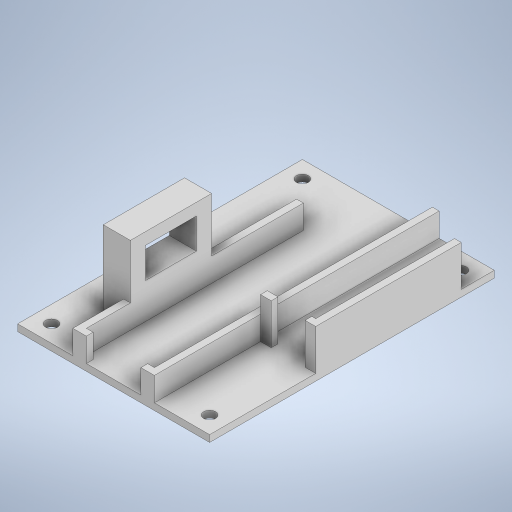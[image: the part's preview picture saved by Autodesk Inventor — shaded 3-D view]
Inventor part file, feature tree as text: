
AUTODESK INVENTOR PART (.ipt)
format: ipt  version: 2023 (Build 270158000, 158)  size: 385,024 bytes
history: native  units: mm
features: extrude x8, sketch x8, other x1
ambient origin geometry x8: Origin, YZ Plane, XZ Plane, XY Plane, X Axis, Y Axis, Z Axis, Center Point
bodies: Body1 (feature_tree)
feature tree (17):
  other  "Sólido1"
  extrude  "Extrusión1"  Depth=20.1mm
  extrude  "Extrusión2"  Depth=2.0mm TaperAngle=0.0deg
  extrude  "Extrusión5"  Depth=7.0mm TaperAngle=0.0deg
  extrude  "Extrusión6"  Depth=15.0mm
  extrude  "Extrusión8"  Depth=2.0mm
  extrude  "Extrusión10"  Depth=4.0mm
  extrude  "Extrusión11"  Depth=14.3mm
  extrude  "Extrusión12"  TaperAngle=0.0deg  [1 undecoded]
  sketch  "Boceto1"  dims[d0=20.1mm d1=80.1mm]
  sketch  "Boceto2"  dims[d2=2.0mm d3=2.0mm d4=0.0mm]
  sketch  "Boceto5"  dims[d5=2.0mm d6=7.0mm d7=0.0mm]
  sketch  "Boceto6"  dims[d8=18.0mm d9=15.0mm]
  sketch  "Boceto8"  dims[d10=12.362696mm d11=2.0mm]
  sketch  "Boceto10"  dims[d12=2.0mm d13=4.0mm]
  sketch  "Boceto11"  dims[d14=4.0mm d25=14.3mm]
  sketch  "Boceto13"  dims[d26=39.0mm d27=0.0mm d28=2.0mm d29=14.0mm d30=0.0mm d31=2.0mm d32=2.0mm d33=2.0mm d34=10.0mm d35=12.0mm d36=0.0mm d44=6.0mm d45=24.0mm d46=0.0mm d47=15.0mm d48=25.0mm d49=0.0mm d57=16.0mm d58=0.0mm d59=15.0mm d60=9.0mm d61=3.5mm d62=3.5mm d63=8.0mm d64=0.0mm d65=0.0mm d66=0.0mm d67=0.0mm d68=0.0mm d72=3.5mm d73=5.0mm d74=5.0mm d75=2.0mm d76=0.0mm]
note: 1 required parameter value undecoded (feature->parameter linkage not recoverable at this tier; creation-order binding heuristic only, values carry confidence <= 0.55)
